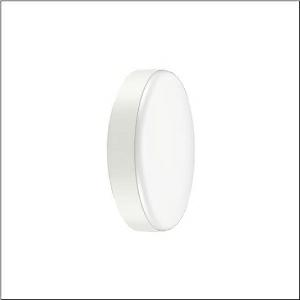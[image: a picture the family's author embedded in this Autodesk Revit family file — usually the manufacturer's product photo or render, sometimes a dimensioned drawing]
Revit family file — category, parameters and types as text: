
# Revit family: round_31_51wc10db34a
name_source: partatom
category: Lighting Fixtures
units: mm (PartAtom-declared; Revit-internal decimal feet)

## family parameters
Cut with Voids When Loaded = No
Host = Face
Light Source = No
Part Type = Normal
Room Calculation Point = No
Round Connector Dimension = Use Diameter
Shared = No

## types (1)
- Round 31 (1 x LED, 4250 lm, 34 W, 3000K)
    Apparent Load = 34 VA
    CIE Flux Codes = 44 75 94 94 100
    Color Rendering = 80
    Color Temperature = 3000K
    Default Elevation = 1800 mm
    Description = Round 31, wall and ceiling luminaire, primary optical cover: cover, of PC, opal, light emission: direct distribution, primary light characteristic: symmetric, installation type: surface-mounted, LED, rated luminous flux: 4.250lm, luminous efficacy: 125lm/W, light colour: 830, colour temperature: 3000K, control gear: DALI 2, with terminal, 5-pole, max. 2.5mm², mains connection: 220..240V, AC, 50/60Hz, rated input power: 34W, luminaire housing, of PC, traffic white (RAL 9016), diameter: 480mm, protection rating (complete): IP65, insulation class (complete): insulation class II (safety insulation), certification: CE, impact resistance: IK10, permissible operating ambient temperature: -20..+40°C, permissible storage temperature: -20..+60°C, packaging unit: 1 piece
    Height = 97 mm
    Lamp = 1 x LED
    Lamp Light Flux = 4250 lm
    Lamp Power = 34 W
    Lamp count = 1
    Length = 480 mm
    Luminous efficacy = 125 lm/W
    Manufacturer = Siteco
    ModVariant = No
    Model = 51WC10DB34A
    Mounting Place = Wall
    Mounting Type = Surface mounted
    Number of Poles = 1
    OnlyDefault = Yes
    Power Factor = 1
    Product Name = Round 31
    Product group = wall and ceiling luminaire | wall mounted
    ProductGroupID = 2001
    Protection Class = Protection class II
    Protection Degree = IP 65
    RLX_Detail_Level = 1
    RLX_Emergency_Light_Flux = 0 lm
    RLX_Emergency_Type = 0
    RLX_Emergency_Type_DB = No
    RlxData = <blob elided: 55369 chars, md5=976a293d>
    Socket = socket
    Standby Power = 0 W
    System Light Flux = 4250 lm
    System Power = 34 W
    Type Comments = Product without accessories
    Type Image = l_1007188.jpg
    URL = http://relux.com
    VarID = ---
    Voltage = 0 V
    Weight = 0.00 kg
    Width = 0 mm  [stored 0 ft]

note: [stored X ft] marks values corroborated as IEEE doubles in the binary element streams (Revit-internal decimal feet)

## geometry (parser evidence)
native form markers: Blend x4, Sweep x12
no freeform markers — native parametric forms only
